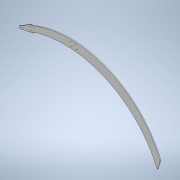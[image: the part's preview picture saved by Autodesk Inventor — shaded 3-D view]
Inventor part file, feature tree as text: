
AUTODESK INVENTOR PART (.ipt)
format: ipt  version: 2020.3 (Build 243373000, 373)  size: 204,800 bytes
history: native  units: mm
features: extrude x7, sketch x7
ambient origin geometry x8: Origin, YZ Plane, XZ Plane, XY Plane, X Axis, Y Axis, Z Axis, Center Point
bodies: Solid1 (feature_tree)
feature tree (14):
  extrude  "Extrusion1"  Depth=40.0mm
  extrude  "Extrusion2"  Depth=465.0mm
  extrude  "Extrusion4"  Depth=4.0mm TaperAngle=0.0deg
  extrude  "Extrusion5"  Depth=4.0mm TaperAngle=0.0deg
  extrude  "Extrusion6"  Depth=10.0mm TaperAngle=0.0deg
  extrude  "Extrusion7"  Depth=25.0mm
  extrude  "Extrusion8"  Depth=4.0mm
  sketch  "Sketch1"  dims[d1=30.0mm d2=40.0mm]
  sketch  "Sketch2"  dims[d4=3.490659mm d5=465.0mm]
  sketch  "Sketch4"  dims[d6=450.0mm d7=4.0mm d8=0.0mm]
  sketch  "Sketch5"  dims[d9=90.0mm d10=4.0mm d11=0.0mm]
  sketch  "Sketch6"  dims[d16=3.490659mm d17=10.0mm d18=0.0mm]
  sketch  "Sketch7"  dims[d19=10.0mm d20=0.0mm d21=25.0mm]
  sketch  "Sketch8"  dims[d22=700.0mm d23=3.0mm d24=3.0mm d25=3.0mm d26=1.256637mm d27=0.383972mm d28=1.361357mm d29=40.0mm d30=80.0mm d31=80.0mm d32=10.0mm d33=0.0mm d34=0.523599mm d35=270.0mm d36=270.0mm d37=3.0mm d38=3.0mm d39=20.0mm d40=19.024089mm d41=3.0mm d42=3.0mm d43=0.174533mm d44=270.0mm d45=0.488692mm d46=10.0mm d47=0.0mm d48=0.488692mm d49=4.0mm d50=0.0mm]
